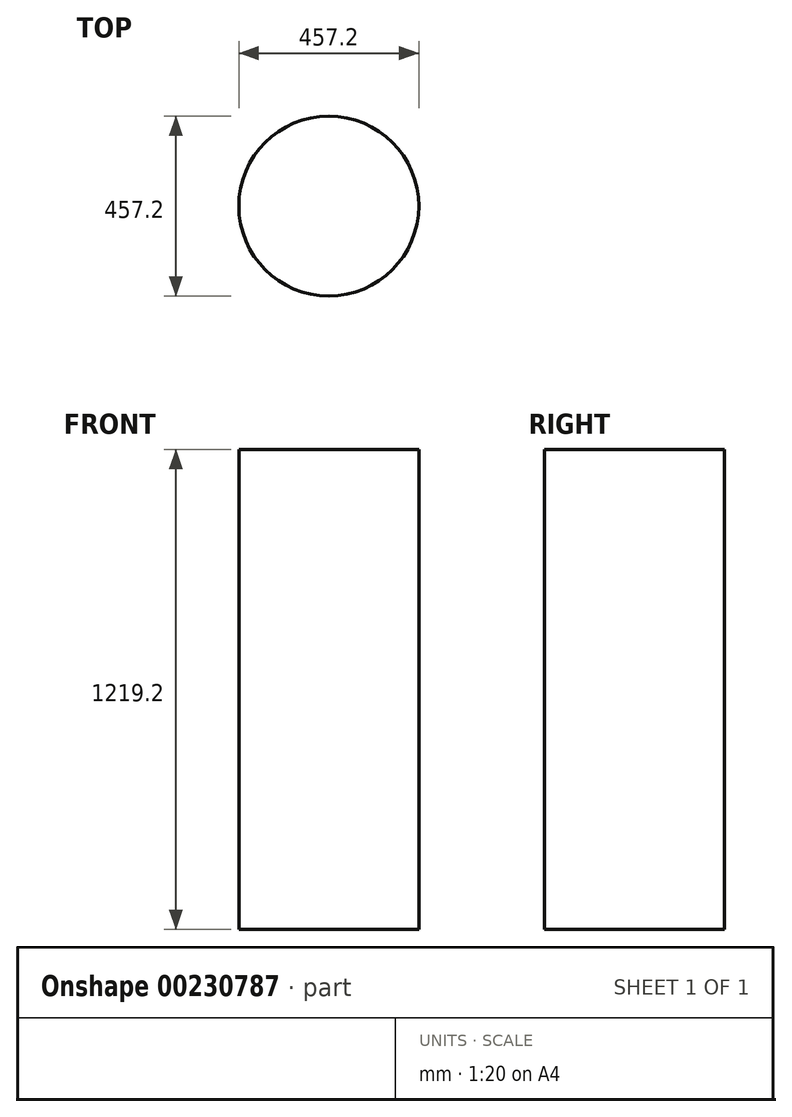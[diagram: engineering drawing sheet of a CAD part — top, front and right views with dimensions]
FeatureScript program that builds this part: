
annotation { "Feature Type Name" : "Feature", "Feature Type Description" : "" }
export const myFeature = defineFeature(function(context is Context, id is Id, definition is map)
    precondition{}
    {
        {
            var Q0;
            Q0=qCreatedBy(makeId("Top.planeOp"),FACE);
            var sketch = newSketch(context, id + "F0", { "sketchPlane" : qUnion([Q0])});
            skCircle(sketch, "E0", {"center": v(-59.85, 41.9) * mm, "radius": 228.6 * mm});
            skSolve(sketch);
        }
        {
            var Q0;
            Q0=makeQuery(id+"F0.imprint","IMPRINT",FACE,{"disambiguationData":[TD([[makeQuery(id+"F0.imprint","IMPRINT",EDGE,{"derivedFrom":sQuery(id+"F0.wireOp",EDGE,"E0")}),1.0]])]});
            extrude(context, id + "F1", {"entities" : qUnion([Q0]), "depth" : 1219.2 * mm});
        }
    });
